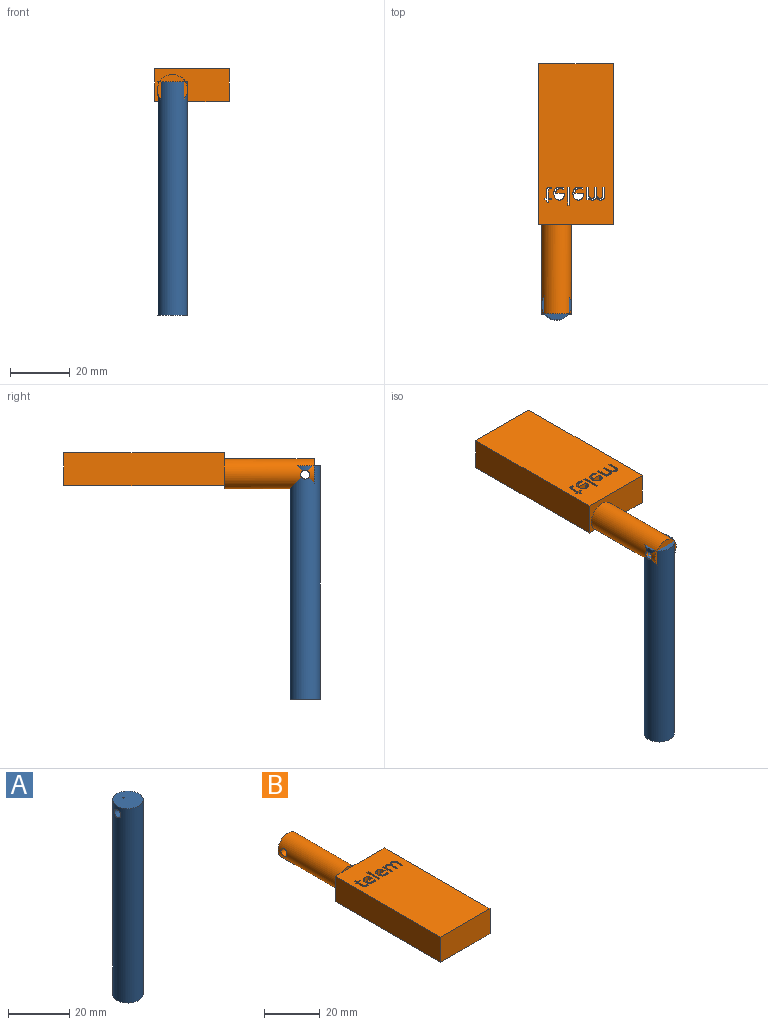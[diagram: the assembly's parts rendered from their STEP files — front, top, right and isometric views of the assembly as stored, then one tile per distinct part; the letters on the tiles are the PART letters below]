
ASSEMBLY  parts=2 mates=1
PART A: 8 faces, bbox 10x10x78 mm
  f0: plane 78x0.49mm, normal (1,0,0), area 38.2mm2, adj f1,f3,f5,f6
  f1: plane 78x0.43mm, normal (0,-1,0), area 33.4mm2, adj f0,f2,f5,f6
  f2: plane 78x0.49mm, normal (-1,0,0), area 38.2mm2, adj f1,f3,f5,f6
  f3: plane 78x0.43mm, normal (0,1,0), area 33.4mm2, adj f0,f2,f5,f6
  f4: cylinder r=5mm len=78mm, axis (0,0,-1), area 2436.1mm2, adj f5,f6,f7
  f5: plane 10x10mm, normal (0,0,1), area 78.3mm2, adj f0,f1,f2,f3,f4
  f6: plane 10x10mm, normal (0,0,-1), area 78.3mm2, adj f0,f1,f2,f3,f4
  f7: cylinder r=1.5mm len=10mm, axis (-1,0,0), area 92.1mm2, adj f4
PART B: 89 faces, bbox 25x83.5x12 mm
  f0: plane 25x11mm, normal (0,-1,0), area 275mm2, adj f1,f82,f83,f84
  f1: plane 53.5x11mm, normal (1,0,0), area 588.5mm2, adj f0,f2,f83,f84
  f2: plane 25x11mm, normal (0,1,0), area 200.5mm2, adj f1,f82,f83,f84,f85
  f3: plane 11x5.95mm, normal (-1,0,0), area 65.4mm2, adj f4,f77,f83,f84
  f4: plane 11x0.63mm, normal (0,1,0), area 7mm2, adj f3,f5,f83,f84
  f5: plane 11x5.95mm, normal (1,0,0), area 65.4mm2, adj f4,f77,f83,f84
  f6: extruded ~11x0.72mm, area 8mm2, adj f7,f78,f83,f84
  f7: extruded ~11x1.47mm, area 17.8mm2, adj f6,f8,f83,f84
  f8: extruded ~11x1.57mm, area 18.7mm2, adj f7,f9,f83,f84
  f9: extruded ~11x1.61mm, area 18.9mm2, adj f8,f10,f83,f84
  f10: extruded ~11x1.34mm, area 16.7mm2, adj f9,f11,f83,f84
  f11: extruded ~11x1.25mm, area 15.3mm2, adj f10,f12,f83,f84
  f12: extruded ~11x1.37mm, area 16.2mm2, adj f11,f13,f83,f84
  f13: plane 11x0.4mm, normal (-1,0,0), area 4.4mm2, adj f12,f14,f83,f84
  f14: plane 11x2.89mm, normal (0,1,0), area 31.7mm2, adj f13,f15,f83,f84
  f15: extruded ~11x1.12mm, area 13.3mm2, adj f14,f16,f83,f84
  f16: extruded ~11x1mm, area 12.1mm2, adj f15,f17,f83,f84
  f17: extruded ~11x1.34mm, area 15.1mm2, adj f16,f18,f83,f84
  f18: plane 11x0.57mm, normal (-1,0,0), area 6.2mm2, adj f17,f78,f83,f84
  f19: plane 11x0.63mm, normal (0,1,0), area 7mm2, adj f20,f79,f83,f84
  f20: plane 11x2.72mm, normal (1,0,0), area 30mm2, adj f19,f21,f83,f84
  f21: extruded ~11x0.75mm, area 8.8mm2, adj f20,f22,f83,f84
  f22: extruded ~11x0.67mm, area 8.1mm2, adj f21,f23,f83,f84
  f23: extruded ~11x0.88mm, area 10.7mm2, adj f22,f24,f83,f84
  f24: extruded ~11x1.05mm, area 12.2mm2, adj f23,f25,f83,f84
  f25: plane 11x2.34mm, normal (-1,0,0), area 25.7mm2, adj f24,f26,f83,f84
  f26: plane 11x0.63mm, normal (0,1,0), area 7mm2, adj f25,f27,f83,f84
  f27: plane 11x2.72mm, normal (1,0,0), area 30mm2, adj f26,f28,f83,f84
  f28: extruded ~11x0.75mm, area 8.8mm2, adj f27,f29,f83,f84
  f29: extruded ~11x0.67mm, area 8.1mm2, adj f28,f30,f83,f84
  f30: extruded ~11x0.87mm, area 10.8mm2, adj f29,f31,f83,f84
  f31: extruded ~11x1.17mm, area 13.5mm2, adj f30,f32,f83,f84
  f32: plane 11x2.2mm, normal (-1,0,0), area 24.2mm2, adj f31,f33,f83,f84
  f33: plane 11x0.63mm, normal (0,1,0), area 7mm2, adj f32,f34,f83,f84
  f34: plane 11x4.19mm, normal (1,0,0), area 46.1mm2, adj f33,f35,f83,f84
  f35: plane 11x0.52mm, normal (0,-1,0), area 5.7mm2, adj f34,f36,f83,f84
  f36: plane 11x0.57mm, normal (-0.98,-0.18,0), area 6.4mm2, adj f35,f37,f83,f84
  f37: plane 11x0.03mm, normal (0,-1,0), area 0.3mm2, adj f36,f38,f83,f84
  f38: extruded ~11x0.51mm, area 7.8mm2, adj f37,f39,f83,f84
  f39: extruded ~11x0.73mm, area 8.4mm2, adj f38,f40,f83,f84
  f40: extruded ~11x1.28mm, area 17.2mm2, adj f39,f41,f83,f84
  f41: plane 11x0.03mm, normal (0,-1,0), area 0.3mm2, adj f40,f42,f83,f84
  f42: extruded ~11x0.54mm, area 8.4mm2, adj f41,f43,f83,f84
  f43: extruded ~11x0.81mm, area 9.3mm2, adj f42,f44,f83,f84
  f44: extruded ~11x1.06mm, area 12.7mm2, adj f43,f45,f83,f84
  f45: extruded ~11x1.17mm, area 13.8mm2, adj f44,f79,f83,f84
  f46: extruded ~11x0.72mm, area 8mm2, adj f47,f80,f83,f84
  f47: extruded ~11x1.47mm, area 17.8mm2, adj f46,f48,f83,f84
  f48: extruded ~11x1.57mm, area 18.7mm2, adj f47,f49,f83,f84
  f49: extruded ~11x1.61mm, area 18.9mm2, adj f48,f50,f83,f84
  f50: extruded ~11x1.34mm, area 16.7mm2, adj f49,f51,f83,f84
  f51: extruded ~11x1.25mm, area 15.3mm2, adj f50,f52,f83,f84
  f52: extruded ~11x1.37mm, area 16.2mm2, adj f51,f53,f83,f84
  f53: plane 11x0.4mm, normal (-1,0,0), area 4.4mm2, adj f52,f54,f83,f84
  f54: plane 11x2.89mm, normal (0,1,0), area 31.7mm2, adj f53,f55,f83,f84
  f55: extruded ~11x1.12mm, area 13.3mm2, adj f54,f56,f83,f84
  f56: extruded ~11x1mm, area 12.1mm2, adj f55,f57,f83,f84
  f57: extruded ~11x1.34mm, area 15.1mm2, adj f56,f58,f83,f84
  f58: plane 11x0.57mm, normal (-1,0,0), area 6.2mm2, adj f57,f80,f83,f84
  f59: extruded ~11x0.49mm, area 6.1mm2, adj f60,f81,f83,f84
  f60: extruded ~11x0.33mm, area 3.6mm2, adj f59,f61,f83,f84
  f61: extruded ~11x0.25mm, area 2.8mm2, adj f60,f62,f83,f84
  f62: plane 11x0.49mm, normal (-1,0,0), area 5.3mm2, adj f61,f63,f83,f84
  f63: extruded ~11x0.3mm, area 3.5mm2, adj f62,f64,f83,f84
  f64: extruded ~11x0.36mm, area 4mm2, adj f63,f65,f83,f84
  f65: extruded ~11x1.28mm, area 22.3mm2, adj f64,f66,f83,f84
  f66: plane 11x2.49mm, normal (1,0,0), area 27.4mm2, adj f65,f67,f83,f84
  f67: plane 11x0.6mm, normal (0,1,0), area 6.6mm2, adj f66,f68,f83,f84
  f68: plane 11x0.31mm, normal (1,0,0), area 3.4mm2, adj f67,f69,f83,f84
  f69: plane 11x0.6mm, normal (0.4,-0.92,0), area 7.2mm2, adj f68,f70,f83,f84
  f70: plane 11x0.89mm, normal (0.96,-0.29,0), area 10.3mm2, adj f69,f71,f83,f84
  f71: plane 11x0.37mm, normal (0,-1,0), area 4mm2, adj f70,f72,f83,f84
  f72: plane 11x0.97mm, normal (-1,0,0), area 10.7mm2, adj f71,f73,f83,f84
  f73: plane 11x1.22mm, normal (0,-1,0), area 13.4mm2, adj f72,f74,f83,f84
  f74: plane 11x0.49mm, normal (-1,0,0), area 5.4mm2, adj f73,f75,f83,f84
  f75: plane 11x1.22mm, normal (0,1,0), area 13.4mm2, adj f74,f76,f83,f84
  f76: plane 11x2.47mm, normal (-1,0,0), area 27.1mm2, adj f75,f81,f83,f84
  f77: plane 11x0.63mm, normal (0,-1,0), area 7mm2, adj f3,f5,f83,f84
  f78: extruded ~11x0.64mm, area 7.4mm2, adj f6,f18,f83,f84
  f79: plane 11x2.73mm, normal (-1,0,0), area 30.1mm2, adj f19,f45,f83,f84
  f80: extruded ~11x0.64mm, area 7.4mm2, adj f46,f58,f83,f84
  f81: extruded ~11x0.58mm, area 6.8mm2, adj f59,f76,f83,f84
  f82: plane 53.5x11mm, normal (-1,0,0), area 588.5mm2, adj f0,f2,f83,f84
  f83: plane 53.5x25mm, normal (0,0,1), area 1300.9mm2, adj f0,f1,f2,f3,f4,f5,f6,f7
  f84: plane 53.5x25mm, normal (0,0,-1), area 1300.9mm2, adj f0,f1,f2,f3,f4,f5,f6,f7
  f85: cylinder r=5mm len=30mm, axis (0,-1,0), area 928.1mm2, adj f2,f86,f87,f88
  f86: plane 10x10mm, normal (0,1,0), area 78.5mm2, adj f85
  f87: plane 6x1mm, normal (0,-1,0), area 4.1mm2, adj f83,f85
  f88: cylinder r=1.5mm len=10mm, axis (1,0,0), area 91.9mm2, adj f85
PLACE A t=(13,-14.35,64.28)mm
PLACE B rot(axis=(1,0,0),180deg) t=(42.77,88.43,146.62)mm
MATE revolute B.f88 <-> A.f7  axis (1,0,0) through (18.06,-14.35,139.28)mm
